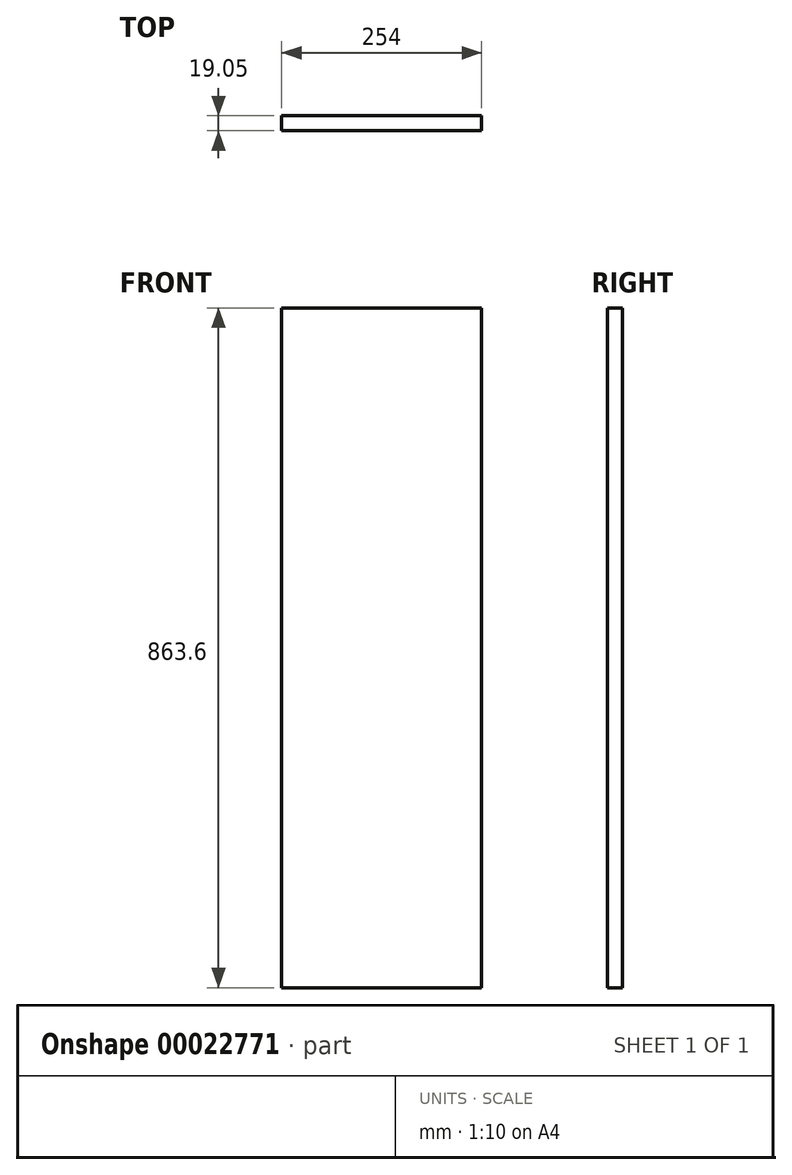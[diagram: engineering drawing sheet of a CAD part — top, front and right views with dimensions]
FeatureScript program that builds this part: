
annotation { "Feature Type Name" : "Feature", "Feature Type Description" : "" }
export const myFeature = defineFeature(function(context is Context, id is Id, definition is map)
    precondition{}
    {
        {
            var Q0;
            Q0=qCreatedBy(makeId("Front.planeOp"),FACE);
            var sketch = newSketch(context, id + "F0", { "sketchPlane" : qUnion([Q0])});
            skLineSegment(sketch, "E0.rect.bottom", {"start": v(127, 431.8) * mm, "end": v(-127, 431.8) * mm});
            skLineSegment(sketch, "E0.rect.top", {"start": v(127, -431.8) * mm, "end": v(-127, -431.8) * mm});
            skLineSegment(sketch, "E0.rect.left", {"start": v(127, 431.8) * mm, "end": v(127, -431.8) * mm});
            skLineSegment(sketch, "E0.rect.right", {"start": v(-127, 431.8) * mm, "end": v(-127, -431.8) * mm});
            skPoint(sketch, "E0.rect.middle", {"position": v(0, 0) * mm});
            skSolve(sketch);
        }
        {
            var Q0;
            Q0=makeQuery(id+"F0.imprint","IMPRINT",FACE,{"disambiguationData":[TD([[makeQuery(id+"F0.imprint","IMPRINT",EDGE,{"derivedFrom":sQuery(id+"F0.wireOp",EDGE,"E0.rect.bottom")}),1.0]])]});
            extrude(context, id + "F1", {"entities" : qUnion([Q0]), "depth" : 19.05 * mm});
        }
    });
